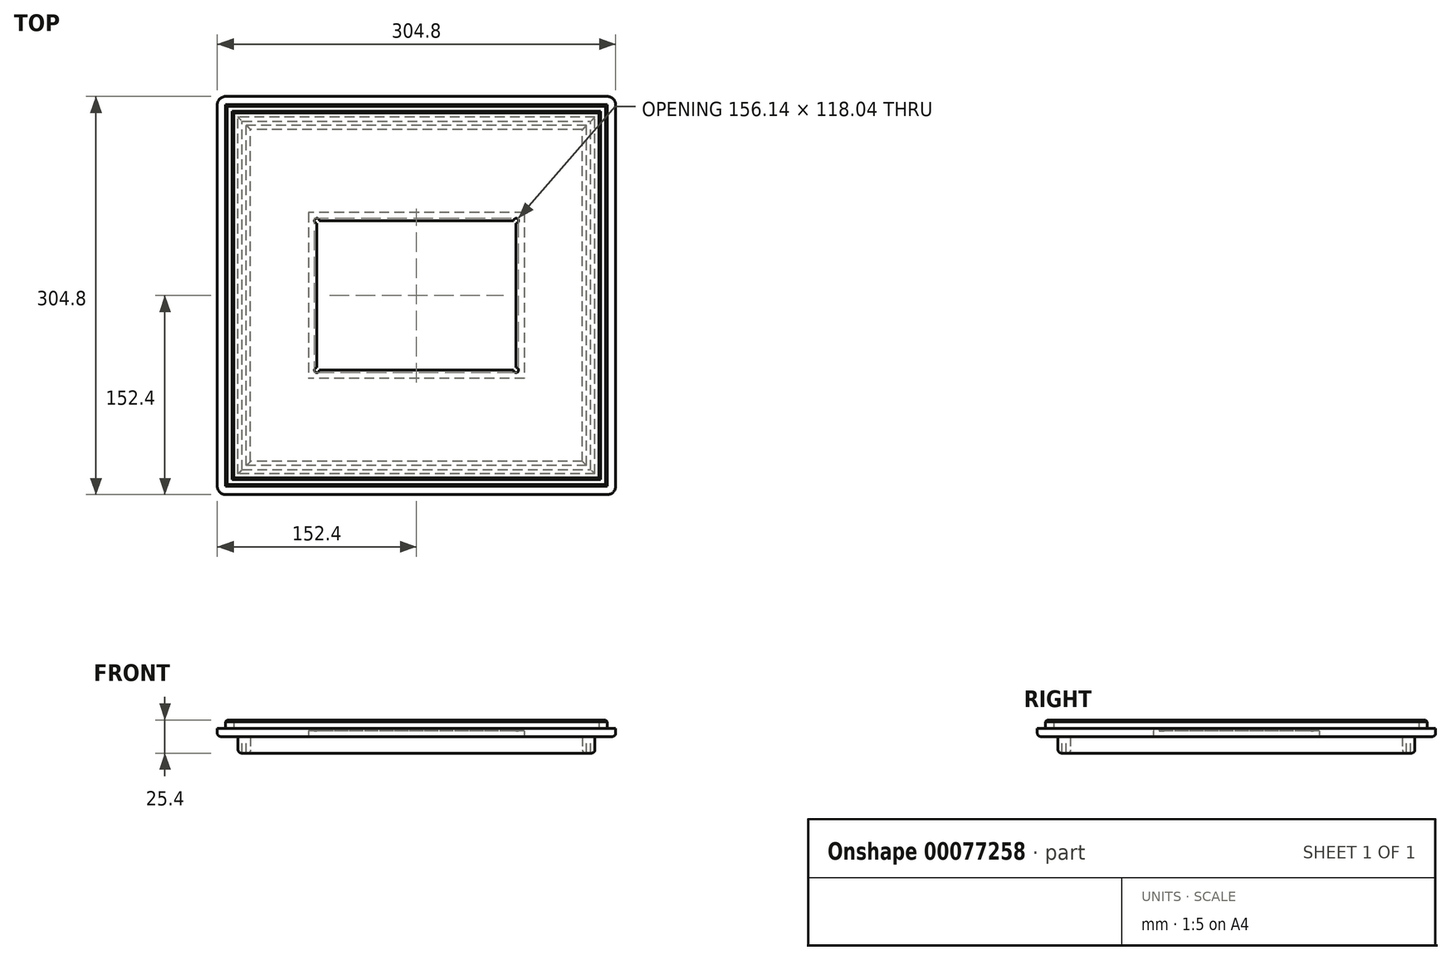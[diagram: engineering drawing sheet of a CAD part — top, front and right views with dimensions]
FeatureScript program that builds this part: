
annotation { "Feature Type Name" : "Feature", "Feature Type Description" : "" }
export const myFeature = defineFeature(function(context is Context, id is Id, definition is map)
    precondition{}
    {
        {
            var Q0;
            Q0=qCreatedBy(makeId("Top.planeOp"),FACE);
            var sketch = newSketch(context, id + "F0", { "sketchPlane" : qUnion([Q0])});
            skLineSegment(sketch, "E0.bottom", {"start": v(152.4, -152.4) * mm, "end": v(-152.4, -152.4) * mm});
            skLineSegment(sketch, "E0.top", {"start": v(152.4, 152.4) * mm, "end": v(-152.4, 152.4) * mm});
            skLineSegment(sketch, "E0.left", {"start": v(152.4, -152.4) * mm, "end": v(152.4, 152.4) * mm});
            skLineSegment(sketch, "E0.right", {"start": v(-152.4, -152.4) * mm, "end": v(-152.4, 152.4) * mm});
            skPoint(sketch, "E0.middle", {"position": v(0, 0) * mm});
            skLineSegment(sketch, "E1.bottom", {"start": v(146.05, -146.05) * mm, "end": v(-146.05, -146.05) * mm});
            skLineSegment(sketch, "E1.top", {"start": v(146.05, 146.05) * mm, "end": v(-146.05, 146.05) * mm});
            skLineSegment(sketch, "E1.left", {"start": v(146.05, -146.05) * mm, "end": v(146.05, 146.05) * mm});
            skLineSegment(sketch, "E1.right", {"start": v(-146.05, -146.05) * mm, "end": v(-146.05, 146.05) * mm});
            skCircle(sketch, "E2", {"center": v(-146.05, 146.05) * mm, "radius": 6.35 * mm});
            skCircle(sketch, "E3", {"center": v(-146.05, -146.05) * mm, "radius": 6.35 * mm});
            skCircle(sketch, "E4", {"center": v(146.05, -146.05) * mm, "radius": 6.35 * mm});
            skCircle(sketch, "E5", {"center": v(146.05, 146.05) * mm, "radius": 6.35 * mm});
            skLineSegment(sketch, "E6.bottom", {"start": v(127, -127) * mm, "end": v(-127, -127) * mm});
            skLineSegment(sketch, "E6.top", {"start": v(127, 127) * mm, "end": v(-127, 127) * mm});
            skLineSegment(sketch, "E6.left", {"start": v(127, -127) * mm, "end": v(127, 127) * mm});
            skLineSegment(sketch, "E6.right", {"start": v(-127, -127) * mm, "end": v(-127, 127) * mm});
            skLineSegment(sketch, "E7.bottom", {"start": v(139.7, 139.7) * mm, "end": v(-139.7, 139.7) * mm});
            skLineSegment(sketch, "E7.top", {"start": v(139.7, -139.7) * mm, "end": v(-139.7, -139.7) * mm});
            skLineSegment(sketch, "E7.left", {"start": v(139.7, 139.7) * mm, "end": v(139.7, -139.7) * mm});
            skLineSegment(sketch, "E7.right", {"start": v(-139.7, 139.7) * mm, "end": v(-139.7, -139.7) * mm});
            skLineSegment(sketch, "E8.bottom", {"start": v(130.18, -130.17) * mm, "end": v(-130.17, -130.18) * mm});
            skLineSegment(sketch, "E8.top", {"start": v(130.18, 130.18) * mm, "end": v(-130.17, 130.18) * mm});
            skLineSegment(sketch, "E8.left", {"start": v(130.18, -130.17) * mm, "end": v(130.18, 130.18) * mm});
            skLineSegment(sketch, "E8.right", {"start": v(-130.17, -130.18) * mm, "end": v(-130.17, 130.17) * mm});
            skLineSegment(sketch, "E9.bottom", {"start": v(136.53, -136.53) * mm, "end": v(-136.52, -136.53) * mm});
            skLineSegment(sketch, "E9.top", {"start": v(136.52, 136.53) * mm, "end": v(-136.53, 136.52) * mm});
            skLineSegment(sketch, "E9.left", {"start": v(136.53, -136.53) * mm, "end": v(136.52, 136.53) * mm});
            skLineSegment(sketch, "E9.right", {"start": v(-136.52, -136.53) * mm, "end": v(-136.53, 136.52) * mm});
            skLineSegment(sketch, "E10.bottom", {"start": v(-133.35, -133.35) * mm, "end": v(133.35, -133.35) * mm});
            skLineSegment(sketch, "E10.top", {"start": v(-133.35, 133.35) * mm, "end": v(133.35, 133.35) * mm});
            skLineSegment(sketch, "E10.left", {"start": v(-133.35, -133.35) * mm, "end": v(-133.35, 133.35) * mm});
            skLineSegment(sketch, "E10.right", {"start": v(133.35, -133.35) * mm, "end": v(133.35, 133.35) * mm});
            skLineSegment(sketch, "E11.bottom", {"start": v(82.55, 63.5) * mm, "end": v(-82.55, 63.5) * mm});
            skLineSegment(sketch, "E11.top", {"start": v(82.55, -63.5) * mm, "end": v(-82.55, -63.5) * mm});
            skLineSegment(sketch, "E11.left", {"start": v(82.55, 63.5) * mm, "end": v(82.55, -63.5) * mm});
            skLineSegment(sketch, "E11.right", {"start": v(-82.55, 63.5) * mm, "end": v(-82.55, -63.5) * mm});
            skLineSegment(sketch, "E12.bottom", {"start": v(76.2, 57.15) * mm, "end": v(-76.2, 57.15) * mm});
            skLineSegment(sketch, "E12.top", {"start": v(76.2, -57.15) * mm, "end": v(-76.2, -57.15) * mm});
            skLineSegment(sketch, "E12.left", {"start": v(76.2, 57.15) * mm, "end": v(76.2, -57.15) * mm});
            skLineSegment(sketch, "E12.right", {"start": v(-76.2, 57.15) * mm, "end": v(-76.2, -57.15) * mm});
            skCircle(sketch, "E13", {"center": v(-76.2, 57.15) * mm, "radius": 1.9 * mm});
            skCircle(sketch, "E14", {"center": v(-76.2, -57.15) * mm, "radius": 1.9 * mm});
            skCircle(sketch, "E15", {"center": v(76.2, -57.15) * mm, "radius": 1.9 * mm});
            skCircle(sketch, "E16", {"center": v(76.2, 57.15) * mm, "radius": 1.9 * mm});
            skSolve(sketch);
        }
        {
            var Q0;
            {var subQ0=sQuery(id+"F0.wireOp",EDGE,"E4");var subQ1=sQuery(id+"F0.wireOp",EDGE,"E0.bottom");var subQ2=makeQuery(id+"F0.imprint","INTERSECT",VERTEX,{"derivedFrom":[subQ1,subQ0]});Q0=makeQuery(id+"F0.imprint","IMPRINT",FACE,{"disambiguationData":[TD([[makeQuery(id+"F0.imprint","IMPRINT",EDGE,{"disambiguationData":[TD([[subQ2,-1.0]])],"derivedFrom":subQ1}),-1.0]])]});}
            var Q1;
            {var subQ0=sQuery(id+"F0.wireOp",EDGE,"E5");var subQ1=sQuery(id+"F0.wireOp",EDGE,"E0.top");var subQ2=makeQuery(id+"F0.imprint","INTERSECT",VERTEX,{"derivedFrom":[subQ1,subQ0]});Q1=makeQuery(id+"F0.imprint","IMPRINT",FACE,{"disambiguationData":[TD([[makeQuery(id+"F0.imprint","IMPRINT",EDGE,{"disambiguationData":[TD([[subQ2,-1.0]])],"derivedFrom":subQ1}),1.0]])]});}
            var Q2;
            {var subQ0=sQuery(id+"F0.wireOp",EDGE,"E4");var subQ1=sQuery(id+"F0.wireOp",EDGE,"E0.left");var subQ2=makeQuery(id+"F0.imprint","INTERSECT",VERTEX,{"derivedFrom":[subQ1,subQ0]});Q2=makeQuery(id+"F0.imprint","IMPRINT",FACE,{"disambiguationData":[TD([[makeQuery(id+"F0.imprint","IMPRINT",EDGE,{"disambiguationData":[TD([[subQ2,-1.0]])],"derivedFrom":subQ1}),1.0]])]});}
            var Q3;
            {var subQ0=sQuery(id+"F0.wireOp",EDGE,"E3");var subQ1=sQuery(id+"F0.wireOp",EDGE,"E0.right");var subQ2=makeQuery(id+"F0.imprint","INTERSECT",VERTEX,{"derivedFrom":[subQ1,subQ0]});Q3=makeQuery(id+"F0.imprint","IMPRINT",FACE,{"disambiguationData":[TD([[makeQuery(id+"F0.imprint","IMPRINT",EDGE,{"disambiguationData":[TD([[subQ2,-1.0]])],"derivedFrom":subQ1}),-1.0]])]});}
            var Q4;
            {var subQ2=sQuery(id+"F0.wireOp",EDGE,"E1.bottom");var subQ5=sQuery(id+"F0.wireOp",EDGE,"E1.left");var subQ7=makeQuery(id+"F0.imprint","INTERSECT",VERTEX,{"derivedFrom":[subQ2,subQ5]});Q4=makeQuery(id+"F0.imprint","IMPRINT",FACE,{"disambiguationData":[TD([[makeQuery(id+"F0.imprint","IMPRINT",EDGE,{"disambiguationData":[TD([[subQ7,-1.0]])],"derivedFrom":subQ2}),1.0]])]});}
            var Q5;
            {var subQ0=sQuery(id+"F0.wireOp",EDGE,"E1.right");var subQ1=sQuery(id+"F0.wireOp",EDGE,"E1.bottom");var subQ2=makeQuery(id+"F0.imprint","INTERSECT",VERTEX,{"derivedFrom":[subQ1,subQ0]});Q5=makeQuery(id+"F0.imprint","IMPRINT",FACE,{"disambiguationData":[TD([[makeQuery(id+"F0.imprint","IMPRINT",EDGE,{"disambiguationData":[TD([[subQ2,1.0]])],"derivedFrom":subQ1}),1.0]])]});}
            var Q6;
            {var subQ2=sQuery(id+"F0.wireOp",EDGE,"E1.top");var subQ5=sQuery(id+"F0.wireOp",EDGE,"E1.left");var subQ6=makeQuery(id+"F0.imprint","INTERSECT",VERTEX,{"derivedFrom":[subQ2,subQ5]});Q6=makeQuery(id+"F0.imprint","IMPRINT",FACE,{"disambiguationData":[TD([[makeQuery(id+"F0.imprint","IMPRINT",EDGE,{"disambiguationData":[TD([[subQ6,-1.0]])],"derivedFrom":subQ2}),-1.0]])]});}
            var Q7;
            Q7=makeQuery(id+"F0.imprint","IMPRINT",FACE,{"disambiguationData":[TD([[makeQuery(id+"F0.imprint","IMPRINT",EDGE,{"derivedFrom":sQuery(id+"F0.wireOp",EDGE,"E6.bottom")}),1.0]])]});
            var Q8;
            {var subQ0=sQuery(id+"F0.wireOp",EDGE,"E1.right");var subQ1=sQuery(id+"F0.wireOp",EDGE,"E1.bottom");var subQ2=makeQuery(id+"F0.imprint","INTERSECT",VERTEX,{"derivedFrom":[subQ1,subQ0]});Q8=makeQuery(id+"F0.imprint","IMPRINT",FACE,{"disambiguationData":[TD([[makeQuery(id+"F0.imprint","IMPRINT",EDGE,{"disambiguationData":[TD([[subQ2,1.0]])],"derivedFrom":subQ1}),-1.0]])]});}
            var Q9;
            {var subQ0=sQuery(id+"F0.wireOp",EDGE,"E1.left");var subQ1=sQuery(id+"F0.wireOp",EDGE,"E1.top");var subQ2=makeQuery(id+"F0.imprint","INTERSECT",VERTEX,{"derivedFrom":[subQ1,subQ0]});Q9=makeQuery(id+"F0.imprint","IMPRINT",FACE,{"disambiguationData":[TD([[makeQuery(id+"F0.imprint","IMPRINT",EDGE,{"disambiguationData":[TD([[subQ2,-1.0]])],"derivedFrom":subQ1}),1.0]])]});}
            var Q10;
            {var subQ3=sQuery(id+"F0.wireOp",EDGE,"E1.top");var subQ5=sQuery(id+"F0.wireOp",EDGE,"E1.right");var subQ6=makeQuery(id+"F0.imprint","INTERSECT",VERTEX,{"derivedFrom":[subQ3,subQ5]});Q10=makeQuery(id+"F0.imprint","IMPRINT",FACE,{"disambiguationData":[TD([[makeQuery(id+"F0.imprint","IMPRINT",EDGE,{"disambiguationData":[TD([[subQ6,1.0]])],"derivedFrom":subQ3}),-1.0]])]});}
            var Q11;
            {var subQ0=sQuery(id+"F0.wireOp",EDGE,"E1.right");var subQ1=sQuery(id+"F0.wireOp",EDGE,"E1.top");var subQ2=makeQuery(id+"F0.imprint","INTERSECT",VERTEX,{"derivedFrom":[subQ1,subQ0]});Q11=makeQuery(id+"F0.imprint","IMPRINT",FACE,{"disambiguationData":[TD([[makeQuery(id+"F0.imprint","IMPRINT",EDGE,{"disambiguationData":[TD([[subQ2,1.0]])],"derivedFrom":subQ1}),1.0]])]});}
            var Q12;
            {var subQ0=sQuery(id+"F0.wireOp",EDGE,"E1.left");var subQ1=sQuery(id+"F0.wireOp",EDGE,"E1.bottom");var subQ2=makeQuery(id+"F0.imprint","INTERSECT",VERTEX,{"derivedFrom":[subQ1,subQ0]});Q12=makeQuery(id+"F0.imprint","IMPRINT",FACE,{"disambiguationData":[TD([[makeQuery(id+"F0.imprint","IMPRINT",EDGE,{"disambiguationData":[TD([[subQ2,-1.0]])],"derivedFrom":subQ1}),-1.0]])]});}
            var Q13;
            Q13=makeQuery(id+"F0.imprint","IMPRINT",FACE,{"disambiguationData":[TD([[makeQuery(id+"F0.imprint","IMPRINT",EDGE,{"derivedFrom":sQuery(id+"F0.wireOp",EDGE,"E7.bottom")}),-1.0]])]});
            var Q14;
            Q14=makeQuery(id+"F0.imprint","IMPRINT",FACE,{"disambiguationData":[TD([[makeQuery(id+"F0.imprint","IMPRINT",EDGE,{"derivedFrom":sQuery(id+"F0.wireOp",EDGE,"E8.bottom")}),1.0]])]});
            var Q15;
            Q15=makeQuery(id+"F0.imprint","IMPRINT",FACE,{"disambiguationData":[TD([[makeQuery(id+"F0.imprint","IMPRINT",EDGE,{"derivedFrom":sQuery(id+"F0.wireOp",EDGE,"E7.bottom")}),1.0]])]});
            var Q16;
            Q16=makeQuery(id+"F0.imprint","IMPRINT",FACE,{"disambiguationData":[TD([[makeQuery(id+"F0.imprint","IMPRINT",EDGE,{"derivedFrom":sQuery(id+"F0.wireOp",EDGE,"E9.bottom")}),-1.0]])]});
            extrude(context, id + "F1", {"entities" : qUnion([Q0, Q1, Q2, Q3, Q4, Q5, Q6, Q7, Q8, Q9, Q10, Q11, Q12, Q13, Q14, Q15, Q16]), "depth" : 6.35 * mm});
        }
        {
            var Q0;
            Q0=makeQuery(id+"F0.imprint","IMPRINT",FACE,{"disambiguationData":[TD([[makeQuery(id+"F0.imprint","IMPRINT",EDGE,{"derivedFrom":sQuery(id+"F0.wireOp",EDGE,"E7.bottom")}),-1.0]])]});
            var Q1;
            {var subQ0=sQuery(id+"F0.wireOp",EDGE,"E1.right");var subQ1=sQuery(id+"F0.wireOp",EDGE,"E1.top");var subQ2=makeQuery(id+"F0.imprint","INTERSECT",VERTEX,{"derivedFrom":[subQ1,subQ0]});Q1=makeQuery(id+"F0.imprint","IMPRINT",FACE,{"disambiguationData":[TD([[makeQuery(id+"F0.imprint","IMPRINT",EDGE,{"disambiguationData":[TD([[subQ2,1.0]])],"derivedFrom":subQ1}),1.0]])]});}
            var Q2;
            {var subQ0=sQuery(id+"F0.wireOp",EDGE,"E1.right");var subQ1=sQuery(id+"F0.wireOp",EDGE,"E1.bottom");var subQ2=makeQuery(id+"F0.imprint","INTERSECT",VERTEX,{"derivedFrom":[subQ1,subQ0]});Q2=makeQuery(id+"F0.imprint","IMPRINT",FACE,{"disambiguationData":[TD([[makeQuery(id+"F0.imprint","IMPRINT",EDGE,{"disambiguationData":[TD([[subQ2,1.0]])],"derivedFrom":subQ1}),-1.0]])]});}
            var Q3;
            {var subQ0=sQuery(id+"F0.wireOp",EDGE,"E1.left");var subQ1=sQuery(id+"F0.wireOp",EDGE,"E1.bottom");var subQ2=makeQuery(id+"F0.imprint","INTERSECT",VERTEX,{"derivedFrom":[subQ1,subQ0]});Q3=makeQuery(id+"F0.imprint","IMPRINT",FACE,{"disambiguationData":[TD([[makeQuery(id+"F0.imprint","IMPRINT",EDGE,{"disambiguationData":[TD([[subQ2,-1.0]])],"derivedFrom":subQ1}),-1.0]])]});}
            var Q4;
            {var subQ0=sQuery(id+"F0.wireOp",EDGE,"E1.left");var subQ1=sQuery(id+"F0.wireOp",EDGE,"E1.top");var subQ2=makeQuery(id+"F0.imprint","INTERSECT",VERTEX,{"derivedFrom":[subQ1,subQ0]});Q4=makeQuery(id+"F0.imprint","IMPRINT",FACE,{"disambiguationData":[TD([[makeQuery(id+"F0.imprint","IMPRINT",EDGE,{"disambiguationData":[TD([[subQ2,-1.0]])],"derivedFrom":subQ1}),1.0]])]});}
            extrude(context, id + "F2", {"entities" : qUnion([Q0, Q1, Q2, Q3, Q4]), "operationType" : NewBodyOperationType.ADD, "depth" : 12.7 * mm});
        }
        {
            var Q0;
            Q0=makeQuery(id+"F2.opExtrude","CAP_EDGE",EDGE,{"disambiguationData":[OSD([sQuery(id+"F0.wireOp",EDGE,"E1.left")])],"isStart":false});
            var Q1;
            Q1=makeQuery(id+"F2.opExtrude","CAP_EDGE",EDGE,{"disambiguationData":[OSD([sQuery(id+"F0.wireOp",EDGE,"E7.left")])],"isStart":false});
            var Q2;
            Q2=makeQuery(id+"F2.opExtrude","CAP_EDGE",EDGE,{"disambiguationData":[OSD([sQuery(id+"F0.wireOp",EDGE,"E7.bottom")])],"isStart":false});
            var Q3;
            Q3=makeQuery(id+"F2.opExtrude","CAP_EDGE",EDGE,{"disambiguationData":[OSD([sQuery(id+"F0.wireOp",EDGE,"E1.top")])],"isStart":false});
            var Q4;
            Q4=makeQuery(id+"F2.opExtrude","CAP_EDGE",EDGE,{"disambiguationData":[OSD([sQuery(id+"F0.wireOp",EDGE,"E7.right")])],"isStart":false});
            var Q5;
            Q5=makeQuery(id+"F2.opExtrude","CAP_EDGE",EDGE,{"disambiguationData":[OSD([sQuery(id+"F0.wireOp",EDGE,"E1.right")])],"isStart":false});
            var Q6;
            Q6=makeQuery(id+"F2.opExtrude","CAP_EDGE",EDGE,{"disambiguationData":[OSD([sQuery(id+"F0.wireOp",EDGE,"E7.top")])],"isStart":false});
            var Q7;
            Q7=makeQuery(id+"F2.opExtrude","CAP_EDGE",EDGE,{"disambiguationData":[OSD([sQuery(id+"F0.wireOp",EDGE,"E1.bottom")])],"isStart":false});
            chamfer(context, id + "F3", {"entities" : qUnion([Q0, Q1, Q2, Q3, Q4, Q5, Q6, Q7]), "width" : 1.27 * mm, "tangentPropagation" : true});
        }
        {
            var Q0;
            Q0=makeQuery(id+"F1.opExtrude","CAP_EDGE",EDGE,{"disambiguationData":[OSD([sQuery(id+"F0.wireOp",EDGE,"E0.bottom")])],"isStart":true});
            var Q1;
            Q1=makeQuery(id+"F1.opExtrude","CAP_EDGE",EDGE,{"disambiguationData":[OSD([sQuery(id+"F0.wireOp",EDGE,"E0.right")])],"isStart":true});
            var Q2;
            Q2=makeQuery(id+"F1.opExtrude","CAP_EDGE",EDGE,{"disambiguationData":[OSD([sQuery(id+"F0.wireOp",EDGE,"E3")])],"isStart":true});
            var Q3;
            Q3=makeQuery(id+"F1.opExtrude","CAP_EDGE",EDGE,{"disambiguationData":[OSD([sQuery(id+"F0.wireOp",EDGE,"E0.left")])],"isStart":true});
            var Q4;
            Q4=makeQuery(id+"F1.opExtrude","CAP_EDGE",EDGE,{"disambiguationData":[OSD([sQuery(id+"F0.wireOp",EDGE,"E4")])],"isStart":true});
            var Q5;
            Q5=makeQuery(id+"F1.opExtrude","CAP_EDGE",EDGE,{"disambiguationData":[OSD([sQuery(id+"F0.wireOp",EDGE,"E0.top")])],"isStart":true});
            var Q6;
            Q6=makeQuery(id+"F1.opExtrude","CAP_EDGE",EDGE,{"disambiguationData":[OSD([sQuery(id+"F0.wireOp",EDGE,"E2")])],"isStart":true});
            var Q7;
            Q7=makeQuery(id+"F1.opExtrude","CAP_EDGE",EDGE,{"disambiguationData":[OSD([sQuery(id+"F0.wireOp",EDGE,"E5")])],"isStart":true});
            fillet(context, id + "F4", {"entities" : qUnion([Q0, Q1, Q2, Q3, Q4, Q5, Q6, Q7]), "radius" : 2.54 * mm, "tangentPropagation" : true, "allowEdgeOverflow" : false});
        }
        {
            var Q0;
            Q0=makeQuery(id+"F0.imprint","IMPRINT",FACE,{"disambiguationData":[TD([[makeQuery(id+"F0.imprint","IMPRINT",EDGE,{"derivedFrom":sQuery(id+"F0.wireOp",EDGE,"E6.bottom")}),1.0]])]});
            var Q1;
            Q1=makeQuery(id+"F0.imprint","IMPRINT",FACE,{"disambiguationData":[TD([[makeQuery(id+"F0.imprint","IMPRINT",EDGE,{"derivedFrom":sQuery(id+"F0.wireOp",EDGE,"E9.bottom")}),-1.0]])]});
            extrude(context, id + "F5", {"entities" : qUnion([Q0, Q1]), "operationType" : NewBodyOperationType.ADD, "oppositeDirection" : true, "depth" : 12.7 * mm});
        }
        {
            var Q0;
            Q0=makeQuery(id+"F5.opExtrude","CAP_EDGE",EDGE,{"disambiguationData":[OSD([sQuery(id+"F0.wireOp",EDGE,"E9.top")])],"isStart":false});
            var Q1;
            Q1=makeQuery(id+"F5.opExtrude","CAP_EDGE",EDGE,{"disambiguationData":[OSD([sQuery(id+"F0.wireOp",EDGE,"E9.right")])],"isStart":false});
            var Q2;
            Q2=makeQuery(id+"F5.opExtrude","CAP_EDGE",EDGE,{"disambiguationData":[OSD([sQuery(id+"F0.wireOp",EDGE,"E9.bottom")])],"isStart":false});
            var Q3;
            Q3=makeQuery(id+"F5.opExtrude","CAP_EDGE",EDGE,{"disambiguationData":[OSD([sQuery(id+"F0.wireOp",EDGE,"E9.left")])],"isStart":false});
            var Q4;
            Q4=makeQuery(id+"F5.opExtrude","CAP_EDGE",EDGE,{"disambiguationData":[OSD([sQuery(id+"F0.wireOp",EDGE,"E6.top")])],"isStart":false});
            var Q5;
            Q5=makeQuery(id+"F5.opExtrude","CAP_EDGE",EDGE,{"disambiguationData":[OSD([sQuery(id+"F0.wireOp",EDGE,"E6.right")])],"isStart":false});
            var Q6;
            Q6=makeQuery(id+"F5.opExtrude","CAP_EDGE",EDGE,{"disambiguationData":[OSD([sQuery(id+"F0.wireOp",EDGE,"E6.bottom")])],"isStart":false});
            var Q7;
            Q7=makeQuery(id+"F5.opExtrude","CAP_EDGE",EDGE,{"disambiguationData":[OSD([sQuery(id+"F0.wireOp",EDGE,"E6.left")])],"isStart":false});
            fillet(context, id + "F6", {"entities" : qUnion([Q0, Q1, Q2, Q3, Q4, Q5, Q6, Q7]), "radius" : 2.54 * mm, "tangentPropagation" : true, "allowEdgeOverflow" : false});
        }
        {
            var Q0;
            Q0=makeQuery(id+"F0.imprint","IMPRINT",FACE,{"disambiguationData":[TD([[makeQuery(id+"F0.imprint","IMPRINT",EDGE,{"derivedFrom":sQuery(id+"F0.wireOp",EDGE,"E6.bottom")}),-1.0]])]});
            var Q1;
            Q1=makeQuery(id+"F0.imprint","IMPRINT",FACE,{"disambiguationData":[TD([[makeQuery(id+"F0.imprint","IMPRINT",EDGE,{"derivedFrom":sQuery(id+"F0.wireOp",EDGE,"E11.bottom")}),1.0]])]});
            extrude(context, id + "F7", {"entities" : qUnion([Q0, Q1]), "operationType" : NewBodyOperationType.ADD, "depth" : 6.35 * mm});
        }
        {
            var Q0;
            Q0=makeQuery(id+"F0.imprint","IMPRINT",FACE,{"disambiguationData":[TD([[makeQuery(id+"F0.imprint","IMPRINT",EDGE,{"derivedFrom":sQuery(id+"F0.wireOp",EDGE,"E11.bottom")}),1.0]])]});
            extrude(context, id + "F8", {"entities" : qUnion([Q0]), "operationType" : NewBodyOperationType.REMOVE, "depth" : 4.44 * mm});
        }
    });
